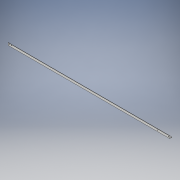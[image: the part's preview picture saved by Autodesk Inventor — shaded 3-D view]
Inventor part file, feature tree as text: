
AUTODESK INVENTOR PART (.ipt)
format: ipt  version: 2017 (Build 210142000, 142)  size: 139,776 bytes
history: native  units: in
note: dims shown in document units (in); Inventor stores cm internally (conversion verified against a paired STEP export)
features: extrude x5, sketch x5
ambient origin geometry x8: Origin, YZ Plane, XZ Plane, XY Plane, X Axis, Y Axis, Z Axis, Center Point
bodies: Solid1 (feature_tree)
feature tree (10):
  extrude  "Extrusion1"  Depth=0.128in
  extrude  "Extrusion2"  Depth=72.0in TaperAngle=0.0deg
  extrude  "Extrusion3"  Depth=0.5in
  extrude  "Extrusion4"  Depth=72.0in TaperAngle=0.0deg
  extrude  "Extrusion5"  Depth=72.0in TaperAngle=0.0deg
  sketch  "Sketch1"  dims[d2=0.128in d3=0.128in]
  sketch  "Sketch2"  dims[d4=1.0in d5=72.0in d6=0.0in]
  sketch  "Sketch3"  dims[d7=0.25in d8=0.5in]
  sketch  "Sketch4"  dims[d9=1.5in d10=72.0in d11=0.0in]
  sketch  "Sketch5"  dims[d12=0.25in d15=72.0in d16=0.0in d17=0.628in d18=10.5in d19=11.5in d20=0.628in d21=0.25in d22=0.5in d23=5.5in d24=72.0in d25=0.0in d26=0.25in d27=0.5in d28=5.5in d29=72.0in d30=0.0in d31=8.5in]
